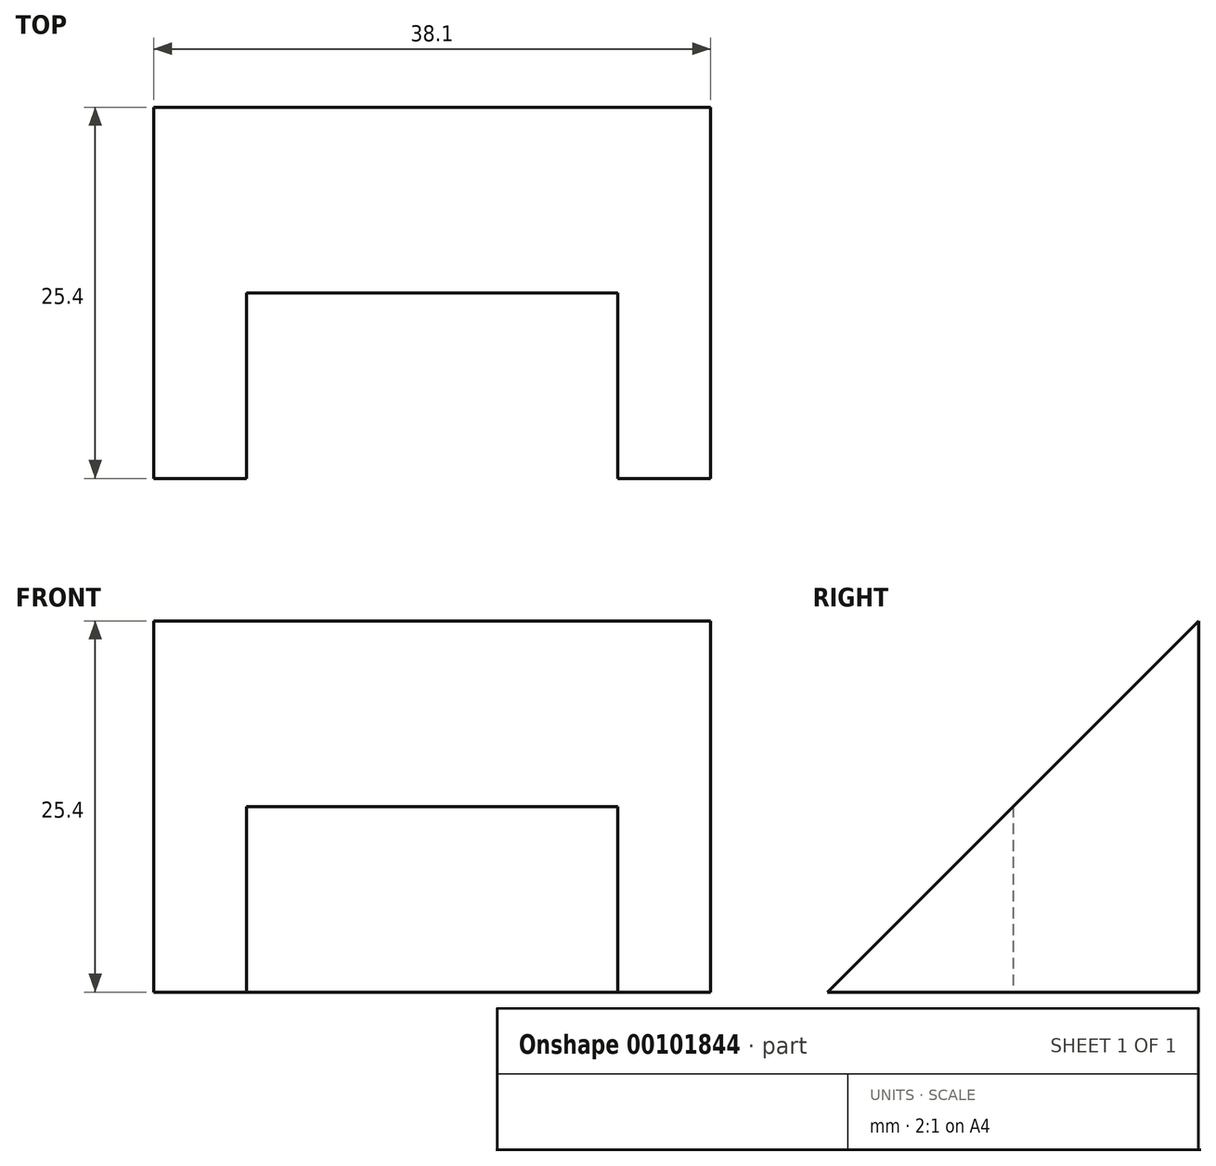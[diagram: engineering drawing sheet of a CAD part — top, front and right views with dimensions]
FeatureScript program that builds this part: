
annotation { "Feature Type Name" : "Feature", "Feature Type Description" : "" }
export const myFeature = defineFeature(function(context is Context, id is Id, definition is map)
    precondition{}
    {
        {
            var Q0;
            Q0=qCreatedBy(makeId("Right.planeOp"),FACE);
            var sketch = newSketch(context, id + "F0", { "sketchPlane" : qUnion([Q0])});
            skLineSegment(sketch, "E0", {"start": v(0, 0) * mm, "end": v(25.4, 0) * mm});
            skLineSegment(sketch, "E1", {"start": v(25.4, 0) * mm, "end": v(25.4, 25.4) * mm});
            skLineSegment(sketch, "E2", {"start": v(25.4, 25.4) * mm, "end": v(0, 0) * mm});
            skSolve(sketch);
        }
        {
            var Q0;
            Q0 = qSketchRegion(id + "F0", true);
            extrude(context, id + "F1", {"entities" : qUnion([Q0]), "oppositeDirection" : true, "depth" : 38.1 * mm});
        }
        {
            var Q0;
            Q0=makeQuery(id+"F1.opExtrude","SWEPT_FACE",FACE,{"disambiguationData":[OSD([sQuery(id+"F0.wireOp",EDGE,"E0")])]});
            var sketch = newSketch(context, id + "F2", { "sketchPlane" : qUnion([Q0])});
            skLineSegment(sketch, "E3.bottom", {"start": v(-31.75, 0) * mm, "end": v(-6.35, 0) * mm});
            skLineSegment(sketch, "E3.top", {"start": v(-31.75, -12.7) * mm, "end": v(-6.35, -12.7) * mm});
            skLineSegment(sketch, "E3.left", {"start": v(-31.75, 0) * mm, "end": v(-31.75, -12.7) * mm});
            skLineSegment(sketch, "E3.right", {"start": v(-6.35, 0) * mm, "end": v(-6.35, -12.7) * mm});
            skSolve(sketch);
        }
        {
            var Q0;
            Q0=makeQuery(id+"F2.imprint","IMPRINT",FACE,{"disambiguationData":[TD([[makeQuery(id+"F2.imprint","IMPRINT",EDGE,{"derivedFrom":sQuery(id+"F2.wireOp",EDGE,"E3.bottom")}),-1.0]])]});
            extrude(context, id + "F3", {"entities" : qUnion([Q0]), "operationType" : NewBodyOperationType.REMOVE, "endBound" : BoundingType.THROUGH_ALL, "oppositeDirection" : true, "depth" : 12.7 * mm});
        }
    });
